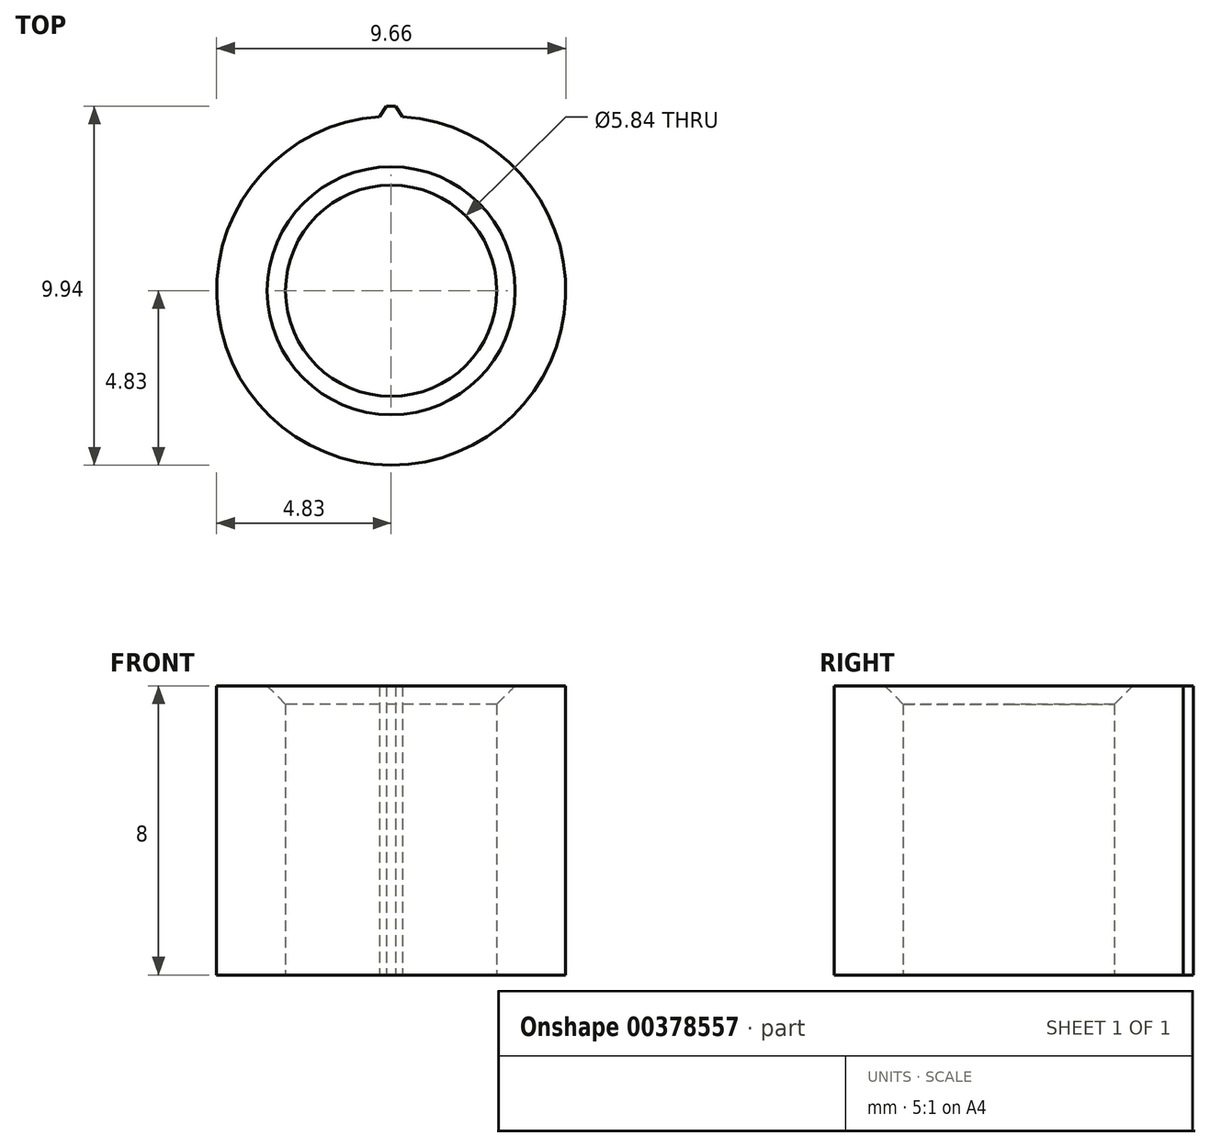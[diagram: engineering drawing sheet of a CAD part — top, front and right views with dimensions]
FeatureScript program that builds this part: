
annotation { "Feature Type Name" : "Feature", "Feature Type Description" : "" }
export const myFeature = defineFeature(function(context is Context, id is Id, definition is map)
    precondition{}
    {
        {
            var Q0;
            Q0=qCreatedBy(makeId("Top.planeOp"),FACE);
            var sketch = newSketch(context, id + "F0", { "sketchPlane" : qUnion([Q0])});
            skCircle(sketch, "E0", {"center": v(0, 0) * mm, "radius": 4.83 * mm});
            skCircle(sketch, "E1", {"center": v(0, 0) * mm, "radius": 2.92 * mm});
            skLineSegment(sketch, "E2", {"start": v(-9.65, 5.1) * mm, "end": v(8.65, 5.1) * mm, "construction": true});
            skLineSegment(sketch, "E3", {"start": v(-11.74, 0) * mm, "end": v(8.56, 0) * mm, "construction": true});
            skLineSegment(sketch, "E4", {"start": v(-0.32, 4.82) * mm, "end": v(-0.13, 5.1) * mm});
            skLineSegment(sketch, "E5", {"start": v(-0.32, 4.82) * mm, "end": v(0.32, 4.82) * mm, "construction": true});
            skLineSegment(sketch, "E6", {"start": v(-0.13, 5.1) * mm, "end": v(0.13, 5.1) * mm});
            skLineSegment(sketch, "E7.trimOffspring", {"start": v(0.13, 5.1) * mm, "end": v(0.32, 4.82) * mm});
            skPoint(sketch, "E8", {"position": v(0, 5.1) * mm});
            skSolve(sketch);
        }
        {
            var Q0;
            Q0=makeQuery(id+"F0.imprint","IMPRINT",FACE,{"disambiguationData":[TD([[makeQuery(id+"F0.imprint","IMPRINT",EDGE,{"derivedFrom":sQuery(id+"F0.wireOp",EDGE,"E1")}),-1.0]])]});
            extrude(context, id + "F1", {"entities" : qUnion([Q0]), "depth" : 8 * mm});
        }
        {
            var Q0;
            {var subQ0=sQuery(id+"F0.wireOp",EDGE,"E4");Q0=makeQuery(id+"F0.imprint","IMPRINT",FACE,{"disambiguationData":[TD([[makeQuery(id+"F0.imprint","IMPRINT",EDGE,{"derivedFrom":subQ0}),-1.0]])]});}
            var Q1;
            Q1=makeQuery(id+"F1.opExtrude","CAP_FACE",FACE,{"disambiguationData":[OSD([sQuery(id+"F0.wireOp",EDGE,"E0"),sQuery(id+"F0.wireOp",EDGE,"E1")])],"isStart":false});
            extrude(context, id + "F2", {"entities" : qUnion([Q0]), "operationType" : NewBodyOperationType.ADD, "endBound" : BoundingType.UP_TO_SURFACE, "endBoundEntityFace" : qUnion([Q1]), "depth" : 25.4 * mm});
        }
        {
            var Q0;
            Q0=makeQuery(id+"F1.opExtrude","CAP_EDGE",EDGE,{"disambiguationData":[OSD([sQuery(id+"F0.wireOp",EDGE,"E1")])],"isStart":false});
            chamfer(context, id + "F3", {"entities" : qUnion([Q0]), "width" : 0.5 * mm, "tangentPropagation" : true});
        }
    });
